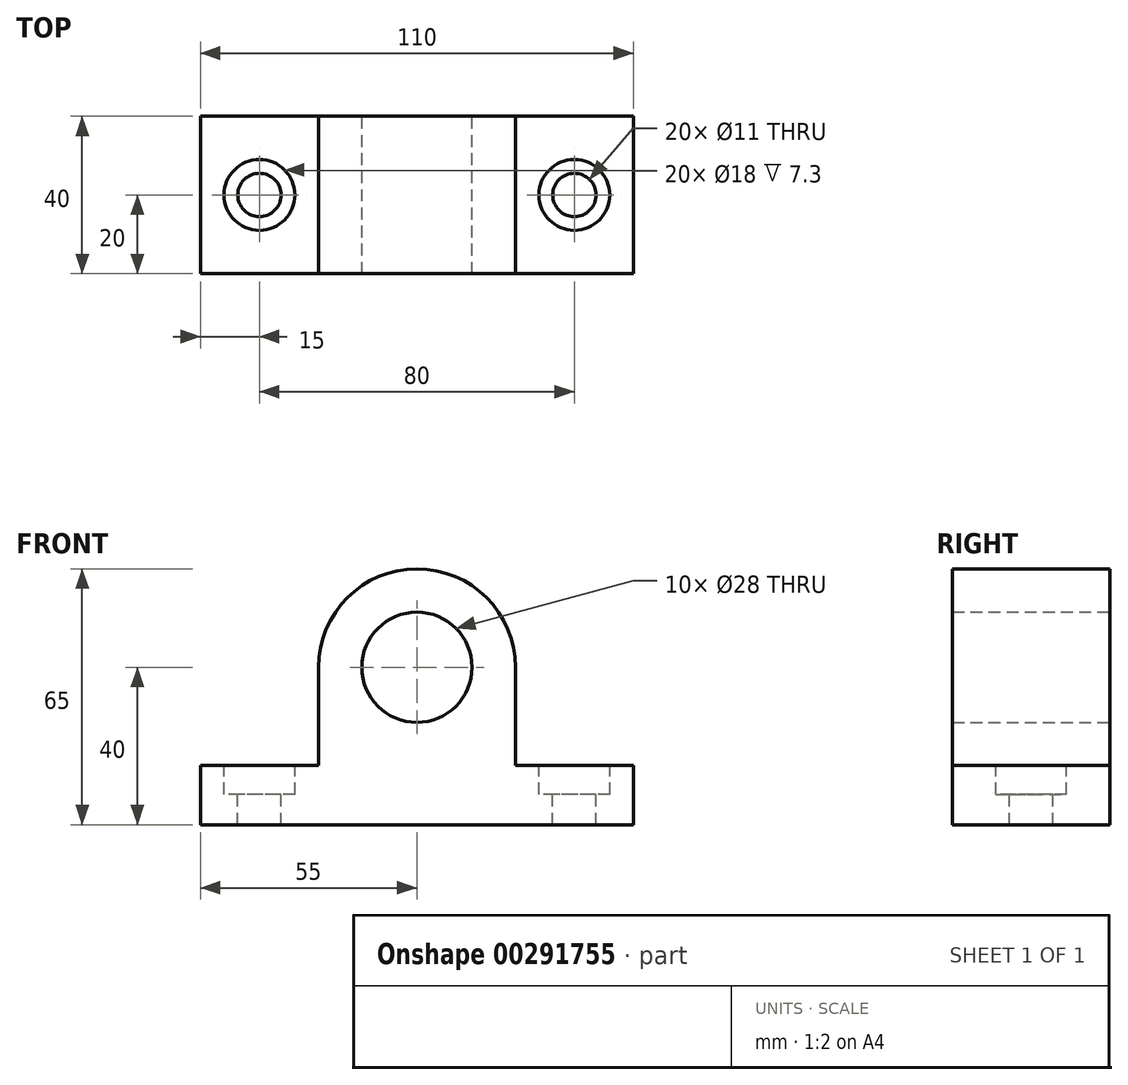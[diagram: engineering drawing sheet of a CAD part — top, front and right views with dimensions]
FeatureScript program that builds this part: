
annotation { "Feature Type Name" : "Feature", "Feature Type Description" : "" }
export const myFeature = defineFeature(function(context is Context, id is Id, definition is map)
    precondition{}
    {
        {
            var Q0;
            Q0=qCreatedBy(makeId("Front.planeOp"),FACE);
            var sketch = newSketch(context, id + "F0", { "sketchPlane" : qUnion([Q0])});
            skLineSegment(sketch, "E0", {"start": v(-55, 0) * mm, "end": v(55, 0) * mm});
            skLineSegment(sketch, "E1", {"start": v(55, 0) * mm, "end": v(55, 15) * mm});
            skLineSegment(sketch, "E2", {"start": v(55, 15) * mm, "end": v(25, 15) * mm});
            skLineSegment(sketch, "E3", {"start": v(25, 15) * mm, "end": v(25, 40) * mm});
            skLineSegment(sketch, "E4", {"start": v(-25, 40) * mm, "end": v(-25, 15) * mm});
            skLineSegment(sketch, "E5", {"start": v(-25, 15) * mm, "end": v(-55, 15) * mm});
            skLineSegment(sketch, "E6", {"start": v(-55, 15) * mm, "end": v(-55, 0) * mm});
            skLineSegment(sketch, "E7", {"start": v(0, 0) * mm, "end": v(0, 40) * mm});
            skArc(sketch, "E8", {"start": v(25, 40) * mm, "mid": v(0, 65) * mm, "end": v(-25, 40) * mm});
            skCircle(sketch, "E9", {"center": v(0, 40) * mm, "radius": 14 * mm});
            skSolve(sketch);
        }
        {
            var Q0;
            Q0 = qSketchRegion(id + "F0", true);
            extrude(context, id + "F1", {"entities" : qUnion([Q0]), "depth" : 40 * mm});
        }
        {
            var Q0;
            Q0=makeQuery(id+"F1.opExtrude","SWEPT_FACE",FACE,{"disambiguationData":[OSD([sQuery(id+"F0.wireOp",EDGE,"E5")])]});
            var sketch = newSketch(context, id + "F2", { "sketchPlane" : qUnion([Q0])});
            skCircle(sketch, "E10", {"center": v(-40, -20) * mm, "radius": 9 * mm});
            skCircle(sketch, "E11", {"center": v(-40, -20) * mm, "radius": 5.5 * mm});
            skCircle(sketch, "E12", {"center": v(40, -20) * mm, "radius": 9 * mm});
            skCircle(sketch, "E13", {"center": v(40, -20) * mm, "radius": 5.5 * mm});
            skPoint(sketch, "E14.start.orphan", {"position": v(-55, -20) * mm});
            skSolve(sketch);
        }
        {
            var Q0;
            Q0=makeQuery(id+"F2.imprint","IMPRINT",FACE,{"disambiguationData":[TD([[makeQuery(id+"F2.imprint","IMPRINT",EDGE,{"derivedFrom":sQuery(id+"F2.wireOp",EDGE,"E11")}),1.0]])]});
            var Q1;
            Q1=makeQuery(id+"F2.imprint","IMPRINT",FACE,{"disambiguationData":[TD([[makeQuery(id+"F2.imprint","IMPRINT",EDGE,{"derivedFrom":sQuery(id+"F2.wireOp",EDGE,"E13")}),1.0]])]});
            extrude(context, id + "F3", {"entities" : qUnion([Q0, Q1]), "operationType" : NewBodyOperationType.REMOVE, "oppositeDirection" : true, "depth" : 25 * mm});
        }
        {
            var Q0;
            Q0=makeQuery(id+"F2.imprint","IMPRINT",FACE,{"disambiguationData":[TD([[makeQuery(id+"F2.imprint","IMPRINT",EDGE,{"derivedFrom":sQuery(id+"F2.wireOp",EDGE,"E10")}),1.0]])]});
            var Q1;
            Q1=makeQuery(id+"F2.imprint","IMPRINT",FACE,{"disambiguationData":[TD([[makeQuery(id+"F2.imprint","IMPRINT",EDGE,{"derivedFrom":sQuery(id+"F2.wireOp",EDGE,"E12")}),1.0]])]});
            extrude(context, id + "F4", {"entities" : qUnion([Q0, Q1]), "operationType" : NewBodyOperationType.REMOVE, "oppositeDirection" : true, "depth" : 7.3 * mm});
        }
    });
